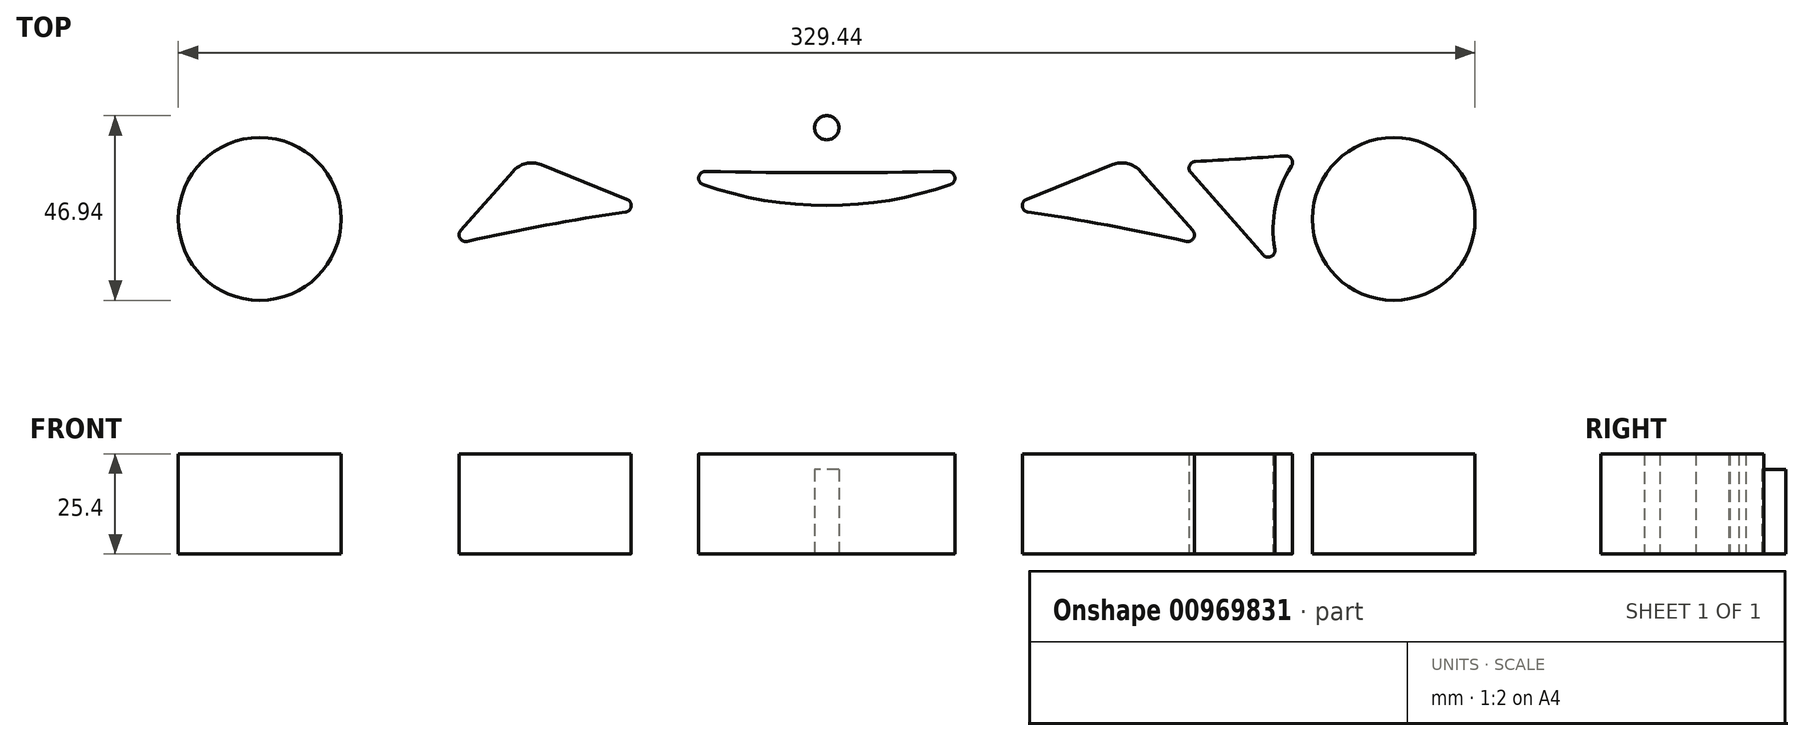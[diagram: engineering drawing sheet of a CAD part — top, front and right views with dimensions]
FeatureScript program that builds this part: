
annotation { "Feature Type Name" : "Feature", "Feature Type Description" : "" }
export const myFeature = defineFeature(function(context is Context, id is Id, definition is map)
    precondition{}
    {
        {
            var Q0;
            Q0=qCreatedBy(makeId("Top.planeOp"),FACE);
            var sketch = newSketch(context, id + "F0", { "sketchPlane" : qUnion([Q0])});
            skCircle(sketch, "E0", {"center": v(0, 0) * mm, "radius": 20.68 * mm});
            skCircle(sketch, "E1", {"center": v(288.09, 0) * mm, "radius": 20.68 * mm});
            skArc(sketch, "E2", {"start": v(261.57, -17.96) * mm, "mid": v(144.04, -2.9) * mm, "end": v(26.52, -17.96) * mm});
            skArc(sketch, "E3", {"start": v(27.52, 16.05) * mm, "mid": v(38.96, 15.29) * mm, "end": v(50.4, 14.6) * mm});
            skLineSegment(sketch, "E4", {"start": v(51.07, -2.9) * mm, "end": v(64.31, 12.12) * mm});
            skLineSegment(sketch, "E5", {"start": v(237.01, -2.9) * mm, "end": v(223.77, 12.12) * mm});
            skLineSegment(sketch, "E6", {"start": v(71.46, 13.81) * mm, "end": v(93.29, 5) * mm});
            skLineSegment(sketch, "E7", {"start": v(216.63, 13.81) * mm, "end": v(194.8, 5) * mm});
            skArc(sketch, "E8", {"start": v(235.36, -5.69) * mm, "mid": v(215.36, -1.55) * mm, "end": v(195.2, 1.73) * mm});
            skArc(sketch, "E9", {"start": v(237.69, 14.6) * mm, "mid": v(249.13, 15.29) * mm, "end": v(260.57, 16.05) * mm});
            skArc(sketch, "E10", {"start": v(113.22, 12.06) * mm, "mid": v(144.04, 11.79) * mm, "end": v(174.87, 12.06) * mm});
            skArc(sketch, "E11", {"start": v(112.62, 8.75) * mm, "mid": v(144.04, 3.4) * mm, "end": v(175.46, 8.75) * mm});
            skArc(sketch, "E12", {"start": v(175.46, 8.75) * mm, "mid": v(176.58, 10.66) * mm, "end": v(174.87, 12.06) * mm});
            skArc(sketch, "E13", {"start": v(113.22, 12.06) * mm, "mid": v(111.5, 10.66) * mm, "end": v(112.62, 8.75) * mm});
            skArc(sketch, "E14", {"start": v(92.89, 1.73) * mm, "mid": v(72.73, -1.55) * mm, "end": v(52.73, -5.69) * mm});
            skArc(sketch, "E15", {"start": v(51.07, -2.9) * mm, "mid": v(50.89, -4.9) * mm, "end": v(52.73, -5.69) * mm});
            skArc(sketch, "E16", {"start": v(92.89, 1.73) * mm, "mid": v(94.34, 3.2) * mm, "end": v(93.29, 5) * mm});
            skArc(sketch, "E17", {"start": v(194.8, 5) * mm, "mid": v(193.75, 3.2) * mm, "end": v(195.2, 1.73) * mm});
            skArc(sketch, "E18", {"start": v(235.36, -5.69) * mm, "mid": v(237.2, -4.9) * mm, "end": v(237.01, -2.9) * mm});
            skArc(sketch, "E19", {"start": v(223.77, 12.12) * mm, "mid": v(220.47, 14.1) * mm, "end": v(216.63, 13.81) * mm});
            skArc(sketch, "E20", {"start": v(71.46, 13.81) * mm, "mid": v(67.62, 14.1) * mm, "end": v(64.31, 12.12) * mm});
            skArc(sketch, "E21", {"start": v(30.2, -7.71) * mm, "mid": v(30.08, 3.26) * mm, "end": v(25.97, 13.44) * mm});
            skLineSegment(sketch, "E22", {"start": v(33.15, -9.13) * mm, "end": v(51.58, 11.77) * mm});
            skArc(sketch, "E23", {"start": v(262.12, 13.44) * mm, "mid": v(258, 3.26) * mm, "end": v(257.88, -7.71) * mm});
            skLineSegment(sketch, "E24", {"start": v(254.93, -9.13) * mm, "end": v(236.5, 11.77) * mm});
            skArc(sketch, "E25", {"start": v(262.12, 13.44) * mm, "mid": v(262.15, 15.22) * mm, "end": v(260.57, 16.05) * mm});
            skArc(sketch, "E26", {"start": v(254.93, -9.13) * mm, "mid": v(256.95, -9.54) * mm, "end": v(257.88, -7.71) * mm});
            skArc(sketch, "E27", {"start": v(237.69, 14.6) * mm, "mid": v(236.21, 13.55) * mm, "end": v(236.5, 11.77) * mm});
            skArc(sketch, "E28", {"start": v(51.58, 11.77) * mm, "mid": v(51.87, 13.55) * mm, "end": v(50.4, 14.6) * mm});
            skArc(sketch, "E29", {"start": v(27.52, 16.05) * mm, "mid": v(25.94, 15.22) * mm, "end": v(25.97, 13.44) * mm});
            skArc(sketch, "E30", {"start": v(30.2, -7.71) * mm, "mid": v(31.14, -9.54) * mm, "end": v(33.15, -9.13) * mm});
            skArc(sketch, "E31", {"start": v(276.37, -23.5) * mm, "mid": v(314.27, -2.03) * mm, "end": v(280.12, 25.03) * mm});
            skArc(sketch, "E32", {"start": v(7.97, 25.03) * mm, "mid": v(-26.19, -2.03) * mm, "end": v(11.72, -23.5) * mm});
            skArc(sketch, "E33", {"start": v(26.52, -17.96) * mm, "mid": v(18.97, -20.34) * mm, "end": v(11.72, -23.5) * mm});
            skLineSegment(sketch, "E34", {"start": v(31.08, 21.44) * mm, "end": v(102.8, 21.44) * mm});
            skCircle(sketch, "E35", {"center": v(144.04, 23.2) * mm, "radius": 3.07 * mm});
            skArc(sketch, "E36", {"start": v(7.97, 25.03) * mm, "mid": v(19.38, 22.34) * mm, "end": v(31.08, 21.44) * mm});
            skArc(sketch, "E37", {"start": v(257.01, 21.44) * mm, "mid": v(268.7, 22.34) * mm, "end": v(280.12, 25.03) * mm});
            skCircle(sketch, "E38", {"center": v(144.04, 23.2) * mm, "radius": 5.96 * mm, "construction": true});
            skArc(sketch, "E39", {"start": v(148.03, 31.07) * mm, "mid": v(144.04, 32.1) * mm, "end": v(140.06, 31.07) * mm});
            skLineSegment(sketch, "E40", {"start": v(257.01, 21.44) * mm, "end": v(185.29, 21.44) * mm});
            skArc(sketch, "E41", {"start": v(276.37, -23.5) * mm, "mid": v(269.11, -20.34) * mm, "end": v(261.57, -17.96) * mm});
            skArc(sketch, "E42", {"start": v(102.99, 21.44) * mm, "mid": v(122.22, 23.9) * mm, "end": v(140.2, 31.14) * mm});
            skArc(sketch, "E43", {"start": v(147.88, 31.14) * mm, "mid": v(165.87, 23.9) * mm, "end": v(185.1, 21.44) * mm});
            skLineSegment(sketch, "E44", {"start": v(106.26, 43.23) * mm, "end": v(138.1, 43.23) * mm, "construction": true});
            skLineSegment(sketch, "E45", {"start": v(106.26, 68.63) * mm, "end": v(140.97, 68.63) * mm, "construction": true});
            skLineSegment(sketch, "E46", {"start": v(138.1, 47.24) * mm, "end": v(140.97, 47.24) * mm, "construction": true});
            skLineSegment(sketch, "E47", {"start": v(147.12, 47.24) * mm, "end": v(147.12, 68.57) * mm, "construction": true});
            skLineSegment(sketch, "E48", {"start": v(140.97, 47.24) * mm, "end": v(140.97, 68.63) * mm, "construction": true});
            skLineSegment(sketch, "E49", {"start": v(149.99, 43.23) * mm, "end": v(149.99, 47.24) * mm, "construction": true});
            skLineSegment(sketch, "E50", {"start": v(138.1, 43.23) * mm, "end": v(138.1, 47.24) * mm, "construction": true});
            skLineSegment(sketch, "E51", {"start": v(147.12, 47.24) * mm, "end": v(149.99, 47.24) * mm, "construction": true});
            skLineSegment(sketch, "E52", {"start": v(149.99, 43.23) * mm, "end": v(195.54, 43.23) * mm, "construction": true});
            skLineSegment(sketch, "E53", {"start": v(147.12, 68.57) * mm, "end": v(195.54, 68.57) * mm, "construction": true});
            skLineSegment(sketch, "E54", {"start": v(144.04, 32.1) * mm, "end": v(144.04, -2.9) * mm, "construction": true});
            skSolve(sketch);
        }
        {
            var Q0;
            Q0 = qSketchRegion(id + "F0", true);
            extrude(context, id + "F1", {"entities" : qUnion([Q0]), "depth" : 25.4 * mm, "offsetDistance" : 25 * mm});
        }
        {
            var Q0;
            Q0=makeQuery(id+"F1.opExtrude","CAP_FACE",FACE,{"disambiguationData":[OSD([sQuery(id+"F0.wireOp",EDGE,"E0"),sQuery(id+"F0.wireOp",EDGE,"E1"),sQuery(id+"F0.wireOp",EDGE,"E2"),sQuery(id+"F0.wireOp",EDGE,"E3"),sQuery(id+"F0.wireOp",EDGE,"E4"),sQuery(id+"F0.wireOp",EDGE,"E5"),sQuery(id+"F0.wireOp",EDGE,"E6"),sQuery(id+"F0.wireOp",EDGE,"E7"),sQuery(id+"F0.wireOp",EDGE,"E8"),sQuery(id+"F0.wireOp",EDGE,"E9"),sQuery(id+"F0.wireOp",EDGE,"E10"),sQuery(id+"F0.wireOp",EDGE,"E11"),sQuery(id+"F0.wireOp",EDGE,"E12"),sQuery(id+"F0.wireOp",EDGE,"E13"),sQuery(id+"F0.wireOp",EDGE,"E14"),sQuery(id+"F0.wireOp",EDGE,"E15"),sQuery(id+"F0.wireOp",EDGE,"E16"),sQuery(id+"F0.wireOp",EDGE,"E17"),sQuery(id+"F0.wireOp",EDGE,"E18"),sQuery(id+"F0.wireOp",EDGE,"E19"),sQuery(id+"F0.wireOp",EDGE,"E20"),sQuery(id+"F0.wireOp",EDGE,"E21"),sQuery(id+"F0.wireOp",EDGE,"E22"),sQuery(id+"F0.wireOp",EDGE,"E23"),sQuery(id+"F0.wireOp",EDGE,"E24"),sQuery(id+"F0.wireOp",EDGE,"E25"),sQuery(id+"F0.wireOp",EDGE,"E26"),sQuery(id+"F0.wireOp",EDGE,"E27"),sQuery(id+"F0.wireOp",EDGE,"E28"),sQuery(id+"F0.wireOp",EDGE,"E29"),sQuery(id+"F0.wireOp",EDGE,"E30"),sQuery(id+"F0.wireOp",EDGE,"E31"),sQuery(id+"F0.wireOp",EDGE,"E32"),sQuery(id+"F0.wireOp",EDGE,"E33"),sQuery(id+"F0.wireOp",EDGE,"E34"),sQuery(id+"F0.wireOp",EDGE,"E35"),sQuery(id+"F0.wireOp",EDGE,"E36"),sQuery(id+"F0.wireOp",EDGE,"E37"),sQuery(id+"F0.wireOp",EDGE,"E39"),sQuery(id+"F0.wireOp",EDGE,"E40"),sQuery(id+"F0.wireOp",EDGE,"E41"),sQuery(id+"F0.wireOp",EDGE,"E42"),sQuery(id+"F0.wireOp",EDGE,"E43")])],"isStart":false});
            var sketch = newSketch(context, id + "F2", { "sketchPlane" : qUnion([Q0])});
            skCircle(sketch, "E55", {"center": v(144.04, 23.2) * mm, "radius": 5.94 * mm});
            skSolve(sketch);
        }
        {
            var Q0;
            Q0 = qSketchRegion(id + "F2", true);
            extrude(context, id + "F3", {"entities" : qUnion([Q0]), "operationType" : NewBodyOperationType.REMOVE, "oppositeDirection" : true, "depth" : 4 * mm, "offsetDistance" : 25 * mm});
        }
    });
